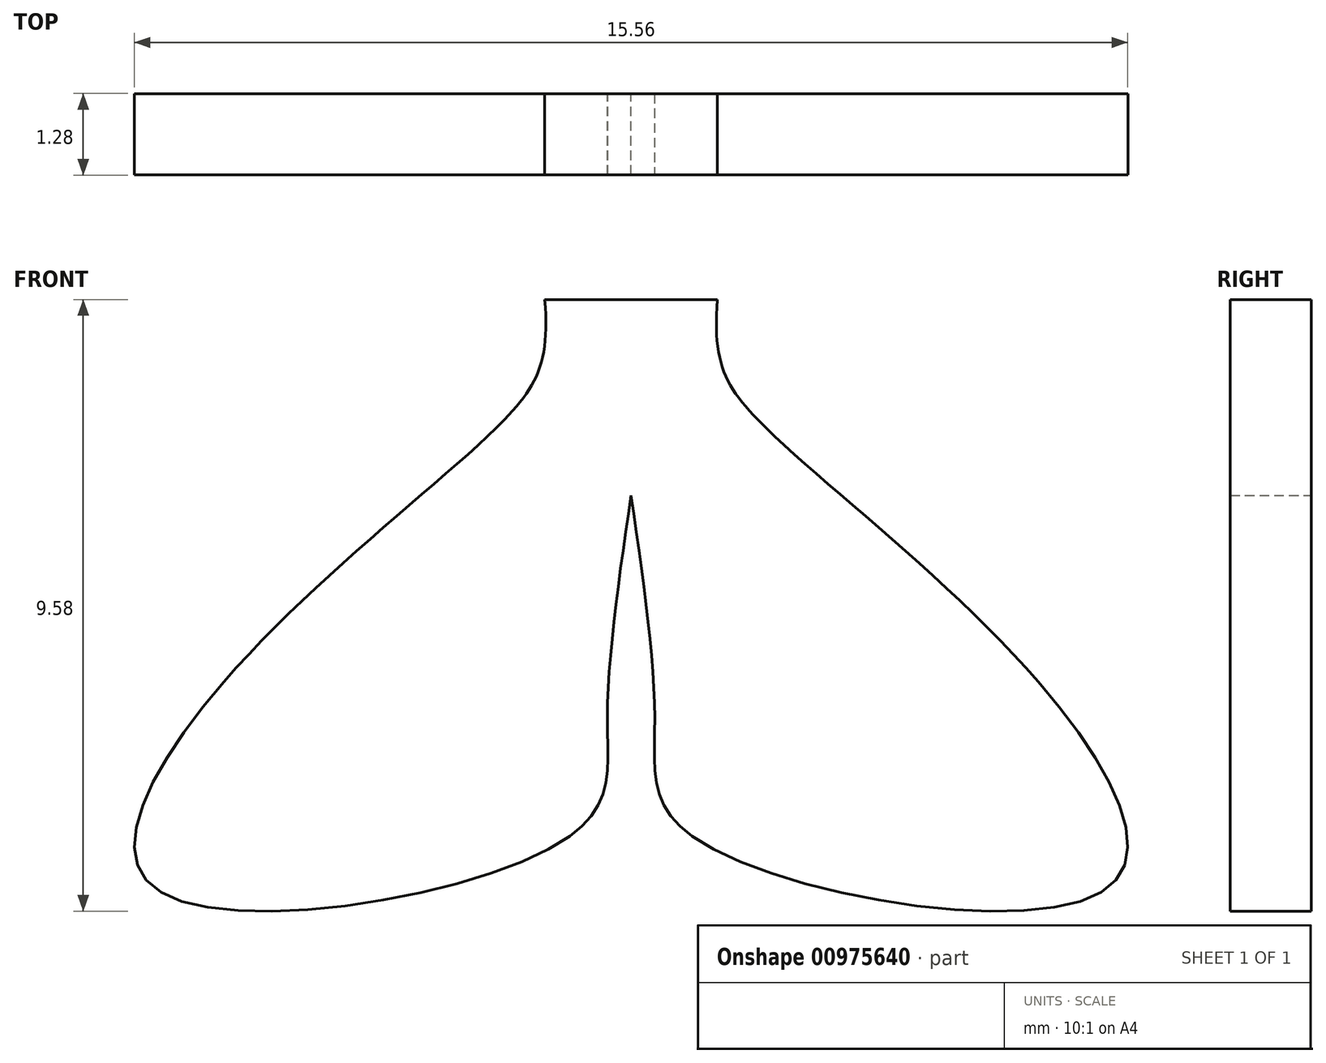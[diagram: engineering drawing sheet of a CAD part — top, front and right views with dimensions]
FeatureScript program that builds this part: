
annotation { "Feature Type Name" : "Feature", "Feature Type Description" : "" }
export const myFeature = defineFeature(function(context is Context, id is Id, definition is map)
    precondition{}
    {
        {
            var Q0;
            Q0=qCreatedBy(makeId("Front.planeOp"),FACE);
            var sketch = newSketch(context, id + "F0", { "sketchPlane" : qUnion([Q0])});
            skFitSpline(sketch, "E0", {"points": [v(0, 33.15) * mm, v(-3.26, 31.1) * mm, v(-5.38, 13.03) * mm, v(-1.35, -8.13) * mm, v(-1.98, -10) * mm, v(-6.38, -14.12) * mm, v(-7.46, -17.35) * mm, v(-0.96, -16.54) * mm, v(-0.37, -14.76) * mm, v(0, -11.2) * mm], "startDerivative": vector(-39.87, -12.63) * mm, "endDerivative": vector(6.67, 45.67) * mm});
            skLineSegment(sketch, "E1", {"start": v(0, -8.13) * mm, "end": v(0, -11.2) * mm});
            skFitSpline(sketch, "E2.MirrorCS", {"points": [v(0, 33.15) * mm, v(3.26, 31.1) * mm, v(5.38, 13.03) * mm, v(1.35, -8.13) * mm, v(1.98, -10) * mm, v(6.38, -14.12) * mm, v(7.46, -17.35) * mm, v(0.96, -16.54) * mm, v(0.37, -14.76) * mm, v(0, -11.2) * mm], "startDerivative": vector(39.87, -12.63) * mm, "endDerivative": vector(-6.67, 45.67) * mm});
            skLineSegment(sketch, "E3", {"start": v(-1.35, -8.13) * mm, "end": v(1.35, -8.13) * mm});
            skLineSegment(sketch, "E4", {"start": v(-1.98, -10) * mm, "end": v(1.98, -10) * mm});
            skFitSpline(sketch, "E5", {"points": [v(-6.38, -14.12) * mm, v(-6.38, -16.52) * mm, v(-0.96, -16.54) * mm], "startDerivative": vector(-1.8, -7.2) * mm, "endDerivative": vector(11.73, 1.76) * mm});
            skFitSpline(sketch, "E6", {"points": [v(6.38, -14.12) * mm, v(6.38, -16.52) * mm, v(0.96, -16.54) * mm], "startDerivative": vector(1.8, -7.2) * mm, "endDerivative": vector(-11.73, 1.76) * mm});
            skSolve(sketch);
        }
        {
            var Q0;
            {var subQ0=sQuery(id+"F0.wireOp",EDGE,"E5");Q0=makeQuery(id+"F0.imprint","IMPRINT",FACE,{"disambiguationData":[TD([[makeQuery(id+"F0.imprint","IMPRINT",EDGE,{"derivedFrom":subQ0}),-1.0]])]});}
            var Q1;
            {var subQ5=sQuery(id+"F0.wireOp",EDGE,"E5");Q1=makeQuery(id+"F0.imprint","IMPRINT",FACE,{"disambiguationData":[TD([[makeQuery(id+"F0.imprint","IMPRINT",EDGE,{"derivedFrom":subQ5}),1.0]])]});}
            var Q2;
            {var subQ0=sQuery(id+"F0.wireOp",EDGE,"E3");var subQ1=sQuery(id+"F0.wireOp",EDGE,"E0");var subQ2=makeQuery(id+"F0.imprint","INTERSECT",VERTEX,{"derivedFrom":[subQ1,subQ0]});Q2=makeQuery(id+"F0.imprint","IMPRINT",FACE,{"disambiguationData":[TD([[makeQuery(id+"F0.imprint","IMPRINT",EDGE,{"disambiguationData":[TD([[subQ2,-1.0]])],"derivedFrom":subQ1}),1.0]])]});}
            var Q3;
            {var subQ6=sQuery(id+"F0.wireOp",EDGE,"E6");Q3=makeQuery(id+"F0.imprint","IMPRINT",FACE,{"disambiguationData":[TD([[makeQuery(id+"F0.imprint","IMPRINT",EDGE,{"derivedFrom":subQ6}),-1.0]])]});}
            var Q4;
            {var subQ0=sQuery(id+"F0.wireOp",EDGE,"E3");var subQ1=sQuery(id+"F0.wireOp",EDGE,"E1");var subQ2=makeQuery(id+"F0.imprint","INTERSECT",VERTEX,{"derivedFrom":[subQ1,subQ0]});Q4=makeQuery(id+"F0.imprint","IMPRINT",FACE,{"disambiguationData":[TD([[makeQuery(id+"F0.imprint","IMPRINT",EDGE,{"disambiguationData":[TD([[subQ2,-1.0]])],"derivedFrom":subQ1}),1.0]])]});}
            var Q5;
            {var subQ0=sQuery(id+"F0.wireOp",EDGE,"E6");Q5=makeQuery(id+"F0.imprint","IMPRINT",FACE,{"disambiguationData":[TD([[makeQuery(id+"F0.imprint","IMPRINT",EDGE,{"derivedFrom":subQ0}),1.0]])]});}
            extrude(context, id + "F1", {"entities" : qUnion([Q0, Q1, Q2, Q3, Q4, Q5]), "depth" : 0.64 * mm, "offsetDistance" : 25.4 * mm, "hasSecondDirection" : true, "secondDirectionOppositeDirection" : true, "secondDirectionDepth" : 0.64 * mm});
        }
    });
